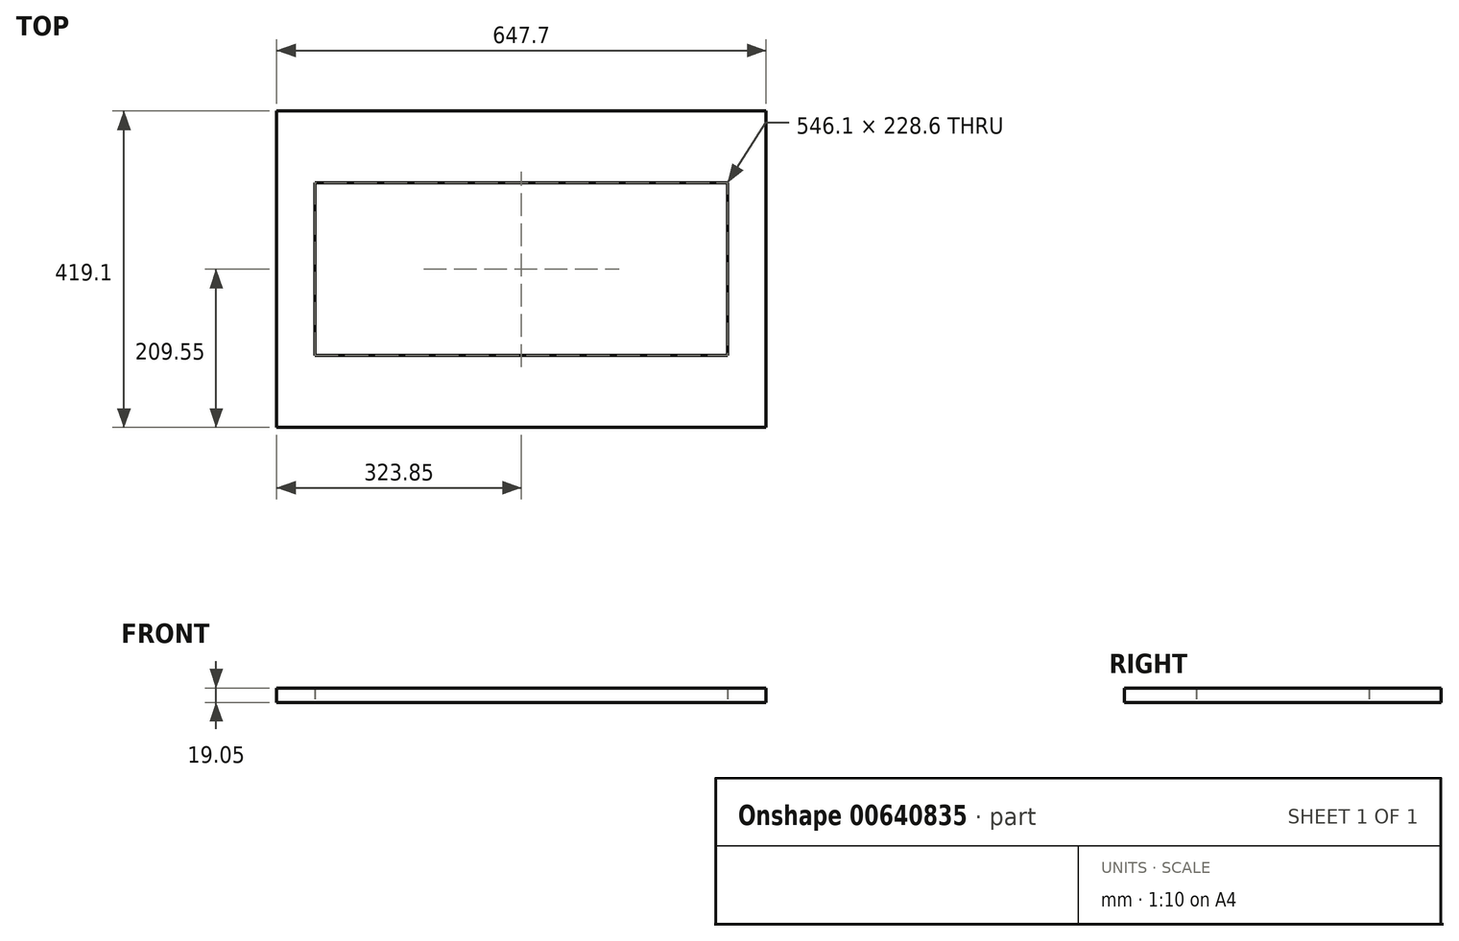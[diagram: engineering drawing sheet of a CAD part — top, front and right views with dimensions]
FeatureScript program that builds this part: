
annotation { "Feature Type Name" : "Feature", "Feature Type Description" : "" }
export const myFeature = defineFeature(function(context is Context, id is Id, definition is map)
    precondition{}
    {
        {
            var Q0;
            Q0=qCreatedBy(makeId("Top.planeOp"),FACE);
            var sketch = newSketch(context, id + "F0", { "sketchPlane" : qUnion([Q0])});
            skLineSegment(sketch, "E0.bottom", {"start": v(-323.85, 209.55) * mm, "end": v(323.85, 209.55) * mm});
            skLineSegment(sketch, "E0.top", {"start": v(-323.85, -209.55) * mm, "end": v(323.85, -209.55) * mm});
            skLineSegment(sketch, "E0.left", {"start": v(-323.85, 209.55) * mm, "end": v(-323.85, -209.55) * mm});
            skLineSegment(sketch, "E0.right", {"start": v(323.85, 209.55) * mm, "end": v(323.85, -209.55) * mm});
            skPoint(sketch, "E0.middle", {"position": v(0, 0) * mm});
            skLineSegment(sketch, "E1.bottom", {"start": v(-273.05, 114.3) * mm, "end": v(273.05, 114.3) * mm});
            skLineSegment(sketch, "E1.top", {"start": v(-273.05, -114.3) * mm, "end": v(273.05, -114.3) * mm});
            skLineSegment(sketch, "E1.left", {"start": v(-273.05, 114.3) * mm, "end": v(-273.05, -114.3) * mm});
            skLineSegment(sketch, "E1.right", {"start": v(273.05, 114.3) * mm, "end": v(273.05, -114.3) * mm});
            skSolve(sketch);
        }
        {
            var Q0;
            Q0=makeQuery(id+"F0.imprint","IMPRINT",FACE,{"disambiguationData":[TD([[makeQuery(id+"F0.imprint","IMPRINT",EDGE,{"derivedFrom":sQuery(id+"F0.wireOp",EDGE,"E0.bottom")}),-1.0]])]});
            extrude(context, id + "F1", {"entities" : qUnion([Q0]), "depth" : 19.05 * mm, "offsetDistance" : 25.4 * mm});
        }
    });
